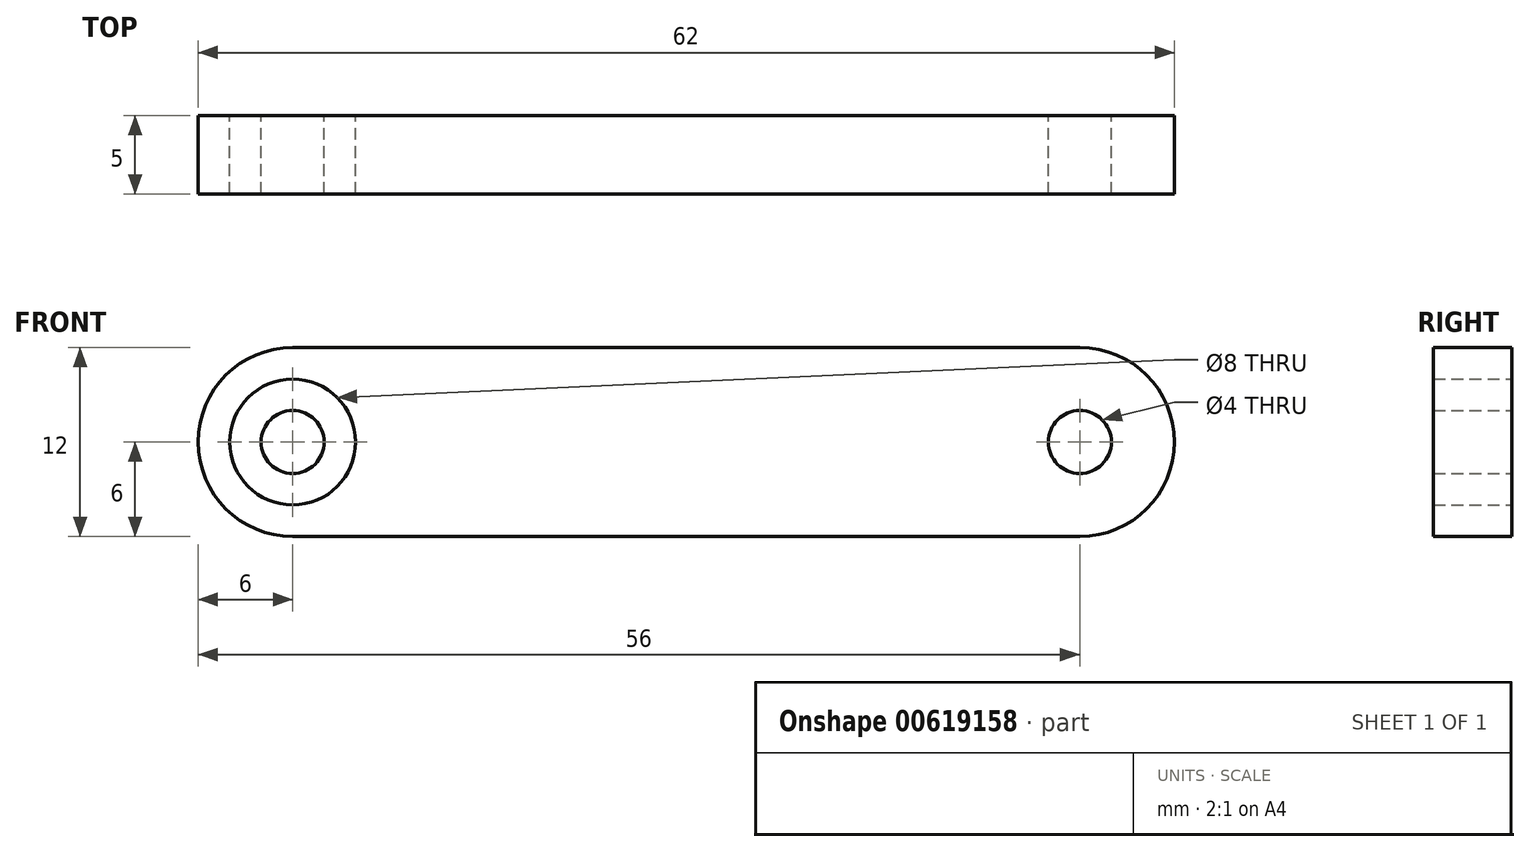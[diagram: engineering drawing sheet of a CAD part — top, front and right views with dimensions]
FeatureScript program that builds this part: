
annotation { "Feature Type Name" : "Feature", "Feature Type Description" : "" }
export const myFeature = defineFeature(function(context is Context, id is Id, definition is map)
    precondition{}
    {
        {
            var Q0;
            Q0=qCreatedBy(makeId("Front.planeOp"),FACE);
            var sketch = newSketch(context, id + "F0", { "sketchPlane" : qUnion([Q0])});
            skLineSegment(sketch, "E0", {"start": v(0, 11.45) * mm, "end": v(0, -14.1) * mm, "construction": true});
            skLineSegment(sketch, "E1", {"start": v(-25, 6) * mm, "end": v(-25, -6) * mm, "construction": true});
            skArc(sketch, "E2", {"start": v(-25, 6) * mm, "mid": v(-31, 0) * mm, "end": v(-25, -6) * mm});
            skCircle(sketch, "E3", {"center": v(-25, 0) * mm, "radius": 4 * mm});
            skCircle(sketch, "E4", {"center": v(-25, 0) * mm, "radius": 2 * mm});
            skLineSegment(sketch, "E5", {"start": v(-25, 6) * mm, "end": v(0, 6) * mm});
            skLineSegment(sketch, "E6", {"start": v(-25, -6) * mm, "end": v(0, -6) * mm});
            skLineSegment(sketch, "E7.MirrorCS", {"start": v(25, 6) * mm, "end": v(0, 6) * mm});
            skLineSegment(sketch, "E8.MirrorCS", {"start": v(25, -6) * mm, "end": v(0, -6) * mm});
            skCircle(sketch, "E9.MirrorC", {"center": v(25, 0) * mm, "radius": 4 * mm});
            skCircle(sketch, "E10.MirrorC", {"center": v(25, 0) * mm, "radius": 2 * mm});
            skArc(sketch, "E11.MirrorCS", {"start": v(25, 6) * mm, "mid": v(31, 0) * mm, "end": v(25, -6) * mm});
            skSolve(sketch);
        }
        {
            var Q0;
            Q0=makeQuery(id+"F0.imprint","IMPRINT",FACE,{"disambiguationData":[TD([[makeQuery(id+"F0.imprint","IMPRINT",EDGE,{"derivedFrom":sQuery(id+"F0.wireOp",EDGE,"E2")}),1.0]])]});
            var Q1;
            Q1=makeQuery(id+"F0.imprint","IMPRINT",FACE,{"disambiguationData":[TD([[makeQuery(id+"F0.imprint","IMPRINT",EDGE,{"derivedFrom":sQuery(id+"F0.wireOp",EDGE,"E4")}),1.0]])]});
            var Q2;
            Q2=makeQuery(id+"F0.imprint","IMPRINT",FACE,{"disambiguationData":[TD([[makeQuery(id+"F0.imprint","IMPRINT",EDGE,{"derivedFrom":sQuery(id+"F0.wireOp",EDGE,"E10.MirrorC")}),-1.0]])]});
            extrude(context, id + "F1", {"entities" : qUnion([Q0, Q1, Q2]), "depth" : 5 * mm, "offsetDistance" : 25 * mm});
        }
    });
